# Revit family: HERZ Strömax Балансировочный клапан с измерительной диафрагмой 4017 ML (LF-MF)
name_source: partatom
category: Rohrzubehör
units: mm (PartAtom-declared; Revit-internal decimal feet)

## family parameters
Arbeitsebenenbasiert = Nein
Beim Laden mit Abzugskörper schneiden = Nein
Bemaßung runder Anschluss = Durchmesser verwenden
Gemeinsam genutzt = Nein
Immer vertikal = Ja
OmniClass-Nummer = 23.65.55.14
OmniClass-Titel = Valves for Liquid Services
Teiletyp = Unterbricht

## types (2) — shared parameters
H02 = 13 mm
Hersteller = HERZ Armaturen Ges.m.b.H.
R01 = 12 mm  [stored 0.0393701 ft]
R02 = 9.5 mm  [stored 0.031168 ft]
R03 = 21.5 mm
S03 = 60 mm  [stored 0.19685 ft]
SCRNCODE = 05;07;02
SCRNSEQ = ARM;ARM_TYP="STRV";2
SW01 = 60.00°
URL = www.herz-armaturen.ru
W01 = 50.00°
Исполнение = Балансировочный клапан ГЕРЦ 4017M с измерительной диафрагмой и двумя измерительными клапанами для измерений перепадов давления наклонный неподнимающийся шпиндель, муфта х муфта, без покрытия, фиксированная воспроизводимая предварительная настройка, показания преднастройки считываются в окошке маховика, с обеих сторон резьбовые муфты, уплотнение шпинделя при помощи тройных уплотнительных колец O-Ring.
Корпус = латунь, устойчивая к селективной цинковой коррозии
Макс. перепад давления на закрытом седле = 1000000.0 Pa
Макс. рабочая температура = 130 °C
Макс. рабочее давление = 2000000.0 Pa
Область применения = Балансировочные клапаны применяются для гидравлической балансировки систем отопления и охлаждения, регулировки магистральных трубопроводов, стояков, теплообменников, регистров отопления и охлаждения.
Среда = Качество теплоносителя должно соответствовать требованиям ONORM H 5195, VDI 2035.
Допускается использование смеси этилен- пропиленгликоля в процентном соотношении 25-50% с водой.
zero-valued in all types: E00, Vorgabe-Ansicht

## per-type parameters (varying)
| type | LF | MF |
| LF | Ja | Nein |
| MF | Nein | Ja |

note: [stored X ft] marks values corroborated as IEEE doubles in the binary element streams (Revit-internal decimal feet)
